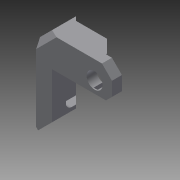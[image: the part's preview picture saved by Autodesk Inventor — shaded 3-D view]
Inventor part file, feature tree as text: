
AUTODESK INVENTOR PART (.ipt)
format: ipt  version: 2015 SP2 (Build 190223200, 223)  size: 124,928 bytes
history: native  units: mm
features: sketch x7, other x3
ambient origin geometry x8: Origin, YZ Plane, XZ Plane, XY Plane, X Axis, Y Axis, Z Axis, Center Point
bodies: Solid1 (feature_tree)
feature tree (10):
  other  "z-axis-top.ipt"
  other  "Solid1::z-axis-top.ipt"
  other  "TaggingFeature1"
  sketch  "Sketch1"  dims[d0=10.0mm]
  sketch  "Sketch2"
  sketch  "Sketch3"
  sketch  "Sketch4"
  sketch  "Sketch5"
  sketch  "Sketch6"
  sketch  "Sketch7"
